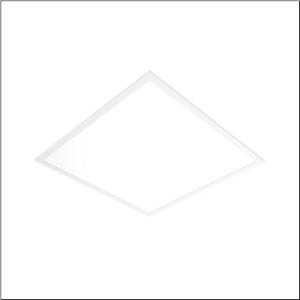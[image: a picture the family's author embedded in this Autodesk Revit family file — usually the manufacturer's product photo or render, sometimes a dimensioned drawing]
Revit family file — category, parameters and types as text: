
# Revit family: apollon_r__41_51mh12w72343_d43e
name_source: partatom
category: Lighting Fixtures
units: mm (PartAtom-declared; Revit-internal decimal feet)

## family parameters
Cut with Voids When Loaded = No
Host = Face
Light Source = No
Part Type = Normal
Room Calculation Point = No
Round Connector Dimension = Use Diameter
Shared = No

## types (1)
- Apollon® 41 (1 x LED, 3500 lm, 28.5 W, 3000K)
    Apparent Load = 29 VA
    CIE Flux Codes = 61 87 97 100 100
    Color Rendering = 80
    Color Temperature = 3000K
    Default Elevation = 1800 mm
    Description = Apollon® 41, office luminaire, primary optical cover: prismatic diffuser, of PS, light emission: direct distribution, primary light characteristic: symmetric, installation type: lay-in mounting, LED, rated luminous flux: 3.500lm, luminous efficacy: 123lm/W, light colour: 830, colour temperature: 3000K, with terminal, 3-pole, mains connection: 220..240V, AC, 50/60Hz, housing, of aluminium section, traffic white (RAL 9016), module: M600, length: 600mm, width: 600mm, height: 28mm, housing upper side, of sheet steel, protection rating (complete): IP20, protection rating (lamp compartment, on room side): IP40, insulation class (complete): insulation class II (safety insulation), certification: CE, ENEC, permissible operating ambient temperature: -25..+40°C, packaging unit: 1 piece
    Height = 0 mm  [stored 0 ft]
    Lamp = 1 x LED
    Lamp Light Flux = 3500 lm
    Lamp Power = 28.5 W
    Lamp count = 1
    Length = 600 mm
    Luminous efficacy = 123 lm/W
    Manufacturer = Siteco
    ModVariant = No
    Model = 51MH12W72343
    Mounting Place = Ceiling
    Mounting Type = Recessed
    Number of Poles = 1
    OnlyDefault = Yes
    Power Factor = 1
    Product Name = Apollon® 41
    Product group = office luminaire | ceiling recessed
    ProductGroupID = 401
    Protection Class = Protection class II
    Protection Degree = IP 20
    RLX_Detail_Level = 1
    RLX_Emergency_Light_Flux = 0 lm
    RLX_Emergency_Type = 0
    RLX_Emergency_Type_DB = No
    RlxData = <blob elided: 12185 chars, md5=49286d9c>
    Socket = socket
    Standby Power = 0 W
    System Light Flux = 3500 lm
    System Power = 29 W
    Type Comments = Product without accessories
    Type Image = l_1291024.jpg
    URL = http://relux.com
    VarID = ---
    Voltage = 0 V
    Weight = 0.00 kg
    Width = 600 mm

note: [stored X ft] marks values corroborated as IEEE doubles in the binary element streams (Revit-internal decimal feet)

## geometry (parser evidence)
native form markers: Sweep x8
no freeform markers — native parametric forms only
